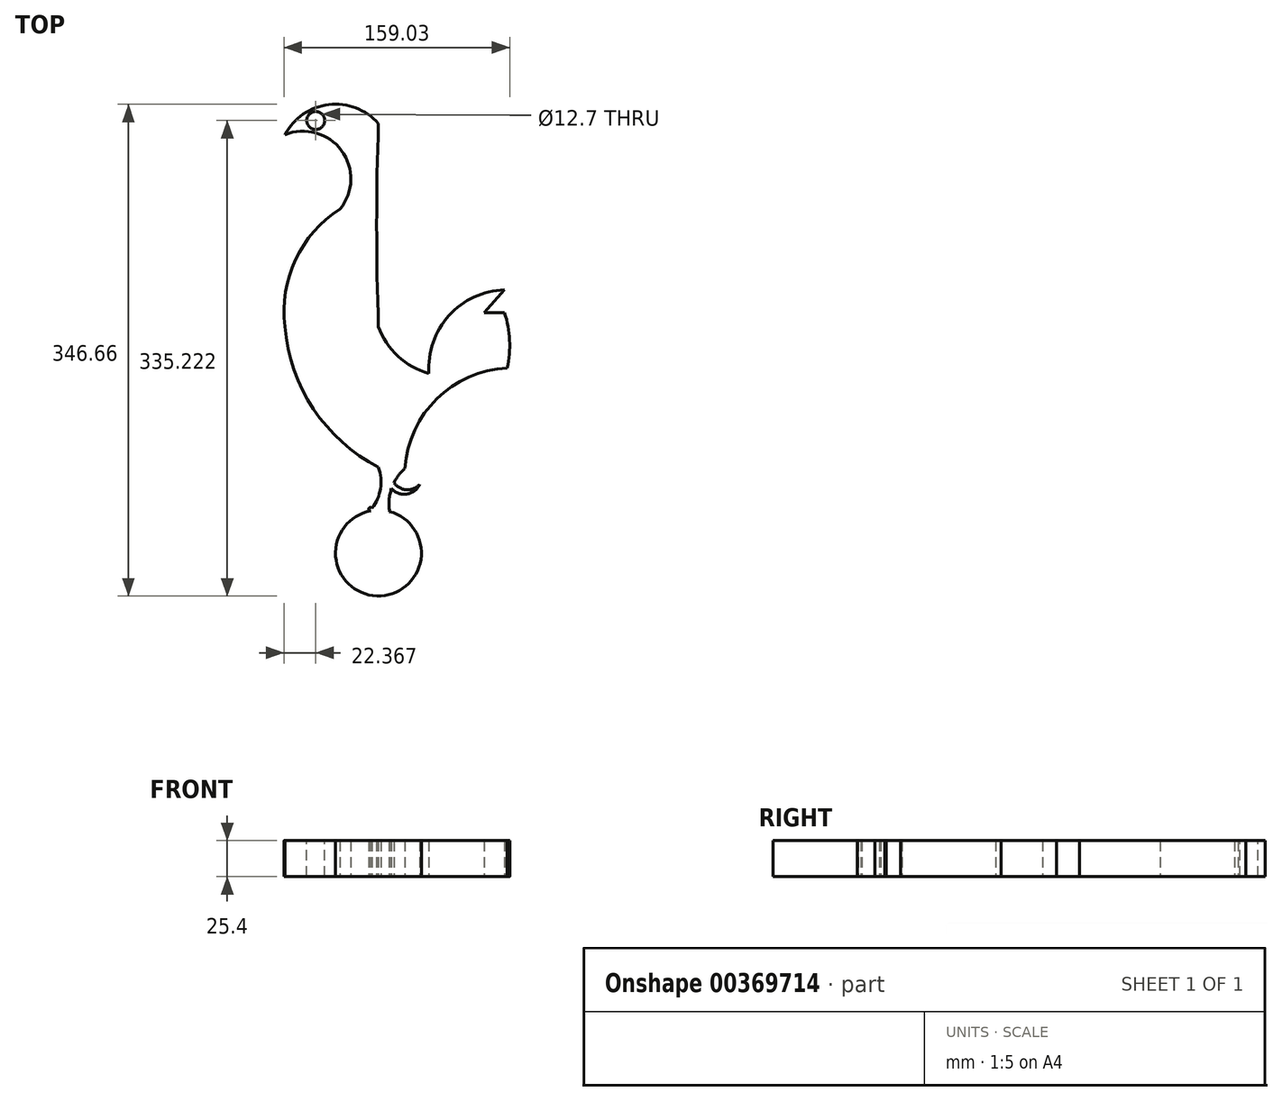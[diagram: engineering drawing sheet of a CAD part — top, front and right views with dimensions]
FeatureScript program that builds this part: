
annotation { "Feature Type Name" : "Feature", "Feature Type Description" : "" }
export const myFeature = defineFeature(function(context is Context, id is Id, definition is map)
    precondition{}
    {
        {
            var Q0;
            Q0=qCreatedBy(makeId("Top.planeOp"),FACE);
            var sketch = newSketch(context, id + "F0", { "sketchPlane" : qUnion([Q0])});
            skArc(sketch, "E0", {"start": v(-4.55, 12.91) * mm, "mid": v(1.41, 26.82) * mm, "end": v(0, 41.9) * mm});
            skArc(sketch, "E1", {"start": v(-65.89, 141.09) * mm, "mid": v(-45.78, 82.96) * mm, "end": v(0, 41.9) * mm});
            skArc(sketch, "E2", {"start": v(-27.04, 223.83) * mm, "mid": v(-58.49, 188.1) * mm, "end": v(-65.89, 141.09) * mm});
            skArc(sketch, "E3", {"start": v(-27.04, 223.83) * mm, "mid": v(-26.08, 265.16) * mm, "end": v(-65.89, 276.35) * mm});
            skArc(sketch, "E4", {"start": v(0, 284.26) * mm, "mid": v(-35, 297.49) * mm, "end": v(-65.89, 276.35) * mm});
            skArc(sketch, "E5", {"start": v(0, 284.26) * mm, "mid": v(-1.26, 212.68) * mm, "end": v(0, 141.09) * mm});
            skArc(sketch, "E6", {"start": v(0, 141.09) * mm, "mid": v(13.73, 120.2) * mm, "end": v(35.56, 108) * mm});
            skArc(sketch, "E7", {"start": v(88.8, 166.99) * mm, "mid": v(49.66, 148.78) * mm, "end": v(35.56, 108) * mm});
            skLineSegment(sketch, "E8", {"start": v(88.8, 166.99) * mm, "end": v(74.4, 150.85) * mm});
            skLineSegment(sketch, "E9", {"start": v(74.4, 150.85) * mm, "end": v(88.8, 150.85) * mm});
            skArc(sketch, "E10", {"start": v(90.69, 111.76) * mm, "mid": v(92.38, 131.44) * mm, "end": v(88.8, 150.85) * mm});
            skArc(sketch, "E11", {"start": v(90.69, 111.76) * mm, "mid": v(41.16, 90.2) * mm, "end": v(18.68, 41.08) * mm});
            skArc(sketch, "E12", {"start": v(18.68, 41.08) * mm, "mid": v(14.3, 36.4) * mm, "end": v(10.9, 30.98) * mm});
            skArc(sketch, "E13", {"start": v(10.9, 30.98) * mm, "mid": v(19.7, 26.04) * mm, "end": v(29.06, 29.82) * mm});
            skArc(sketch, "E14", {"start": v(9.2, 26.9) * mm, "mid": v(19.92, 22.94) * mm, "end": v(29.06, 29.82) * mm});
            skArc(sketch, "E15.trimOffspring", {"start": v(9.2, 26.9) * mm, "mid": v(7.51, 18.83) * mm, "end": v(7.86, 10.59) * mm});
            skArc(sketch, "E16", {"start": v(-5.56, 11.11) * mm, "mid": v(-1.18, -48.86) * mm, "end": v(7.86, 10.59) * mm});
            skArc(sketch, "E17", {"start": v(-4.55, 12.91) * mm, "mid": v(-6.71, 12.94) * mm, "end": v(-5.56, 11.11) * mm});
            skSolve(sketch);
        }
        {
            var Q0;
            Q0 = qSketchRegion(id + "F0", true);
            extrude(context, id + "F1", {"entities" : qUnion([Q0]), "depth" : 25.4 * mm});
        }
        {
            var Q0;
            Q0=makeQuery(id+"F1.opExtrude","CAP_FACE",FACE,{"disambiguationData":[OSD([sQuery(id+"F0.wireOp",EDGE,"E0"),sQuery(id+"F0.wireOp",EDGE,"E1"),sQuery(id+"F0.wireOp",EDGE,"E2"),sQuery(id+"F0.wireOp",EDGE,"E3"),sQuery(id+"F0.wireOp",EDGE,"E4"),sQuery(id+"F0.wireOp",EDGE,"E5"),sQuery(id+"F0.wireOp",EDGE,"E6"),sQuery(id+"F0.wireOp",EDGE,"E7"),sQuery(id+"F0.wireOp",EDGE,"E8"),sQuery(id+"F0.wireOp",EDGE,"E9"),sQuery(id+"F0.wireOp",EDGE,"E10"),sQuery(id+"F0.wireOp",EDGE,"E11"),sQuery(id+"F0.wireOp",EDGE,"E12"),sQuery(id+"F0.wireOp",EDGE,"E13"),sQuery(id+"F0.wireOp",EDGE,"E14"),sQuery(id+"F0.wireOp",EDGE,"E15.trimOffspring"),sQuery(id+"F0.wireOp",EDGE,"E16"),sQuery(id+"F0.wireOp",EDGE,"E17")])],"isStart":false});
            var sketch = newSketch(context, id + "F2", { "sketchPlane" : qUnion([Q0])});
            skCircle(sketch, "E18", {"center": v(-44.2, 286.34) * mm, "radius": 6.35 * mm});
            skSolve(sketch);
        }
        {
            var Q0;
            Q0 = qSketchRegion(id + "F2", true);
            extrude(context, id + "F3", {"entities" : qUnion([Q0]), "operationType" : NewBodyOperationType.REMOVE, "oppositeDirection" : true, "depth" : 25.4 * mm});
        }
    });
